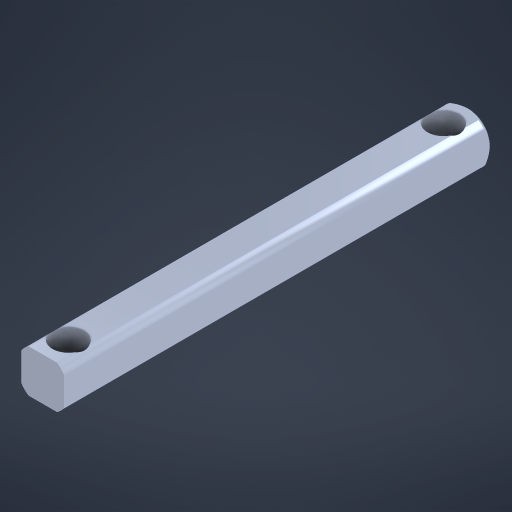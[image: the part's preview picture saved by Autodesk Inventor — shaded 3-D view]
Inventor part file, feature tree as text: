
AUTODESK INVENTOR PART (.ipt)
format: ipt  version: 2024 (Build 280153000, 153)  size: 311,808 bytes
history: native  units: in
note: dims shown in document units (in); Inventor stores cm internally (conversion verified against a paired STEP export)
features: other x50, sketch x3, extrude x2, thicken_offset x1, hole x1
ambient origin geometry x8: Origin, YZ Plane, XZ Plane, XY Plane, X Axis, Y Axis, Z Axis, Center Point
bodies: Solid1 (feature_tree)
feature tree (57):
  other  "Table"
  other  "Shaft HS 0.5 in"
  other  "Shaft HS 1.0 in"
  other  "Shaft HS 1.5 in"
  other  "Shaft HS 2.0 in"
  other  "Shaft HS 2.5 in"
  other  "Shaft HS 3.0 in"
  other  "Shaft HS 3.5 in"
  other  "Shaft HS 4.0 in"
  other  "Shaft HS 4.5 in"
  other  "Shaft HS 5.0 in"
  other  "Shaft HS 5.5 in"
  other  "Shaft HS 6.0 in"
  other  "Shaft HS 6.5 in"
  other  "Shaft HS 7.0 in"
  other  "Shaft HS 7.5 in"
  other  "Shaft HS 8.0 in"
  other  "Shaft HS 8.5 in"
  other  "Shaft HS 9.0 in"
  other  "Shaft HS 9.5 in"
  other  "Shaft HS 10.0 in"
  other  "Shaft HS 10.5 in"
  other  "Shaft HS 11.0 in"
  other  "Shaft HS 11.5 in"
  other  "Shaft HS 12.0 in"
  other  "Shaft HS 12.5 in"
  other  "Shaft HS 13.0 in"
  other  "Shaft HS 13.5 in"
  other  "Shaft HS 14.0 in"
  other  "Shaft HS 14.5 in"
  other  "Shaft HS 15.0 in"
  other  "Shaft HS 15.5 in"
  other  "Shaft HS 16.0 in"
  other  "Shaft HS 16.5 in"
  other  "Shaft HS 17.0 in"
  other  "Shaft HS 17.5 in"
  other  "Shaft HS 18.0 in"
  other  "Shaft HS 18.5 in"
  other  "Shaft HS 19.0 in"
  other  "Shaft HS 19.5 in"
  other  "Shaft HS 20.0 in"
  other  "Shaft HS 20.5 in"
  other  "Shaft HS 21.0 in"
  other  "Shaft HS 21.5 in"
  other  "Shaft HS 22.0 in"
  other  "Shaft HS 22.5 in"
  other  "Shaft HS 23.0 in"
  other  "Shaft HS 23.5 in"
  other  "Shaft HS 24.0 in"
  extrude  "Extrusion1"  Depth=12.1875in
  thicken_offset  "Thicken1"
  extrude  "Extrusion2"  Depth=21.625in
  hole  "Hole1"  [1 undecoded]
  sketch  "Sketch2"  dims[d0=0.0625in d1=0.0in d2=12.1875in]
  sketch  "Sketch3"  dims[d3=12.125in d4=21.625in]
  sketch  "Sketch6"  dims[d5=0.0in d9=0.15in d10=0.15in d11=0.1875in d12=0.75in d13=0.375in d14=0.25in d15=0.5635in d16=1.0in d17=0.8108in]
  other  "Cut-Revolve3"
note: 1 required parameter value undecoded (feature->parameter linkage not recoverable at this tier; creation-order binding heuristic only, values carry confidence <= 0.55)
